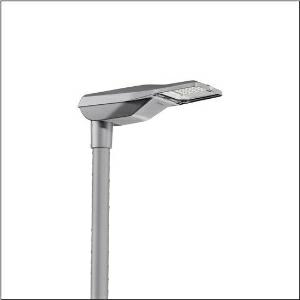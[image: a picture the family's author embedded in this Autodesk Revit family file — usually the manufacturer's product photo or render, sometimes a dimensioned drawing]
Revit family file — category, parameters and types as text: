
# Revit family: streetlight_sl_21_iq_micro___stw1_0a_5xe1e41d08cb_a1a9
name_source: partatom
category: Lighting Fixtures
units: mm (PartAtom-declared; Revit-internal decimal feet)

## family parameters
Cut with Voids When Loaded = No
Host = Face
Light Source = No
Part Type = Normal
Room Calculation Point = No
Round Connector Dimension = Use Diameter
Shared = No

## types (1)
- --- (1 x LED, 2980 lm, 19.4 W, 4000K)
    Apparent Load = 19 VA
    CIE Flux Codes = 38 75 98 100 100
    Color Rendering = 70
    Color Temperature = 4000K
    Default Elevation = 1800 mm
    Description = Streetlight SL 21 iQ micro, mast luminaire, primary light control with lens, of PMMA, primary optical cover: cover, of toughened safety glass, transparent, light distribution: STW1.0a, light emission: direct distribution, primary light characteristic: asymmetric, installation type: post-top, side-entry, LED, High Power LED, rated luminous flux: 2.980lm, luminous efficacy: 154lm/W, light colour: 740, colour temperature: 4000K, control gear: iQ-Comfort, control: Auto-Match, Temp-Guard, Lumen-Switch, Night-Set, Smart-Wire, Light-Fading, Desk-Remote (wireless, voltage-free reading and setting of iQ features in the workshop via application-optimized NFC function/RFID function), optimised constant luminous flux control (CLO 2.0), pre-setting: linear dimming characteristic, mains connection: 220..240V, AC, 50/60Hz, start of lifetime: 19W, end of service life: 20W, reduction: 10W, luminaire housing, of diecast aluminium, powder-coated, Siteco® metallic grey (DB 702S), corrosivity category C5 mid according to DIN EN ISO 12944, please order mast flange separately, inclination adjustable: 0°, 5°, 10°, 15°, sealing non-destructively replaceable, multi-level sealing system, length: 528mm, width: 235mm, height: 110mm, mast flange for spigot size: 42mm (side-entry): 5XC10008XM4, 60/48mm (side-entry/post-top): 5XC10108XM2, 76/60mm (side-entry/post-top): 5XC10108XM1, protection rating (complete): IP66, insulation class (complete): insulation class II (safety insulation), certification: CE, ENEC, ENEC+, VDE, impact resistance: IK10, permissible operating ambient temperature for outdoor applications: -40..+50°C, standard-compliant lighting for roads and squares, packaging unit: 1 piece

Light Distribution: STW1.0a
    Height = 110 mm
    Lamp = 1 x LED
    Lamp Light Flux = 2980 lm
    Lamp Power = 19.4 W
    Lamp count = 1
    Length = 528 mm
    Luminous efficacy = 154 lm/W
    Manufacturer = Siteco
    ModVariant = No
    Model = 5XE1E41D08CB
    Number of Poles = 1
    OnlyDefault = Yes
    Power Factor = 1
    Product Name = Streetlight SL 21 iQ micro | STW1.0a
    Product group = mast luminaire | pylon top
    ProductGroupID = 6100
    Protection Class = Protection class II
    Protection Degree = IP 66
    RLX_Detail_Level = 1
    RLX_Emergency_Light_Flux = 0 lm
    RLX_Emergency_Type = 0
    RLX_Emergency_Type_DB = No
    RlxData = <blob elided: 98653 chars, md5=ecaaba6d>
    Socket = socket
    Standby Power = 0 W
    System Light Flux = 2980 lm
    System Power = 19 W
    Type Comments = factory setting: luminous flux: 100 % | dim-lin: 254 | 387 mA
    Type Image = l_1006881.jpg
    URL = http://relux.com
    VarID = @adj_160303
    Voltage = 0 V
    Weight = 0.00 kg
    Width = 235 mm

## geometry (parser evidence)
native form markers: Blend x4, Sweep x10
no freeform markers — native parametric forms only
